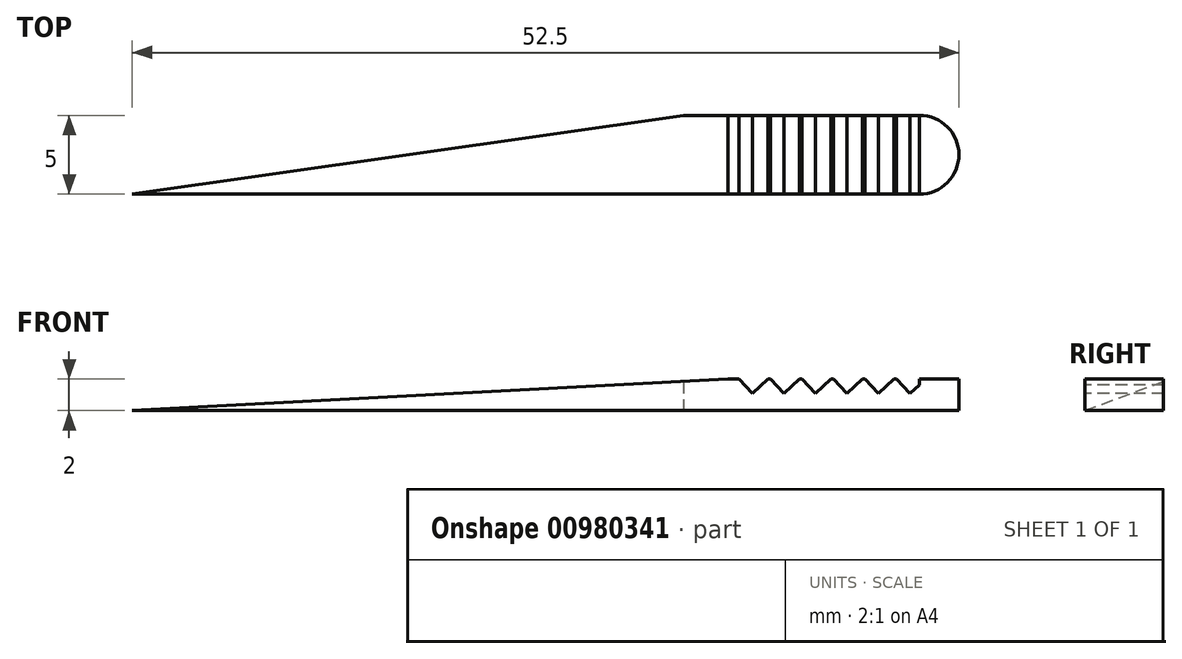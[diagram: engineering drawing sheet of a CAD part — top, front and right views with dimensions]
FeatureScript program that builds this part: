
annotation { "Feature Type Name" : "Feature", "Feature Type Description" : "" }
export const myFeature = defineFeature(function(context is Context, id is Id, definition is map)
    precondition{}
    {
        {
            var Q0;
            Q0=qCreatedBy(makeId("Top.planeOp"),FACE);
            var sketch = newSketch(context, id + "F0", { "sketchPlane" : qUnion([Q0])});
            skLineSegment(sketch, "E0", {"start": v(-50, 0) * mm, "end": v(0, 0) * mm});
            skLineSegment(sketch, "E1", {"start": v(0, 5) * mm, "end": v(-15, 5) * mm});
            skLineSegment(sketch, "E2", {"start": v(-15, 5) * mm, "end": v(-50, 0) * mm});
            skArc(sketch, "E3", {"start": v(0, 0) * mm, "mid": v(2.5, 2.5) * mm, "end": v(0, 5) * mm});
            skSolve(sketch);
        }
        {
            var Q0;
            Q0=makeQuery(id+"F0.imprint","IMPRINT",FACE,{"disambiguationData":[TD([[makeQuery(id+"F0.imprint","IMPRINT",EDGE,{"derivedFrom":sQuery(id+"F0.wireOp",EDGE,"E0")}),1.0]])]});
            extrude(context, id + "F1", {"entities" : qUnion([Q0]), "depth" : 2 * mm, "offsetDistance" : 25 * mm});
        }
        {
            var Q0;
            Q0=makeQuery(id+"F1.opExtrude","SWEPT_FACE",FACE,{"disambiguationData":[OSD([sQuery(id+"F0.wireOp",EDGE,"E0")])]});
            var sketch = newSketch(context, id + "F2", { "sketchPlane" : qUnion([Q0])});
            skLineSegment(sketch, "E4", {"start": v(-50, 0) * mm, "end": v(-12.17, 2) * mm});
            skSolve(sketch);
        }
        {
            var Q0;
            {var subQ0=sQuery(id+"F2.wireOp",EDGE,"E4");Q0=makeQuery(id+"F2.imprint","IMPRINT",FACE,{"disambiguationData":[TD([[makeQuery(id+"F2.imprint","IMPRINT",EDGE,{"derivedFrom":subQ0}),1.0]])]});}
            extrude(context, id + "F3", {"entities" : qUnion([Q0]), "operationType" : NewBodyOperationType.REMOVE, "oppositeDirection" : true, "depth" : 5 * mm, "offsetDistance" : 25 * mm});
        }
        {
            var Q0;
            Q0=makeQuery(id+"F1.opExtrude","SWEPT_FACE",FACE,{"disambiguationData":[OSD([sQuery(id+"F0.wireOp",EDGE,"E0")])]});
            var sketch = newSketch(context, id + "F4", { "sketchPlane" : qUnion([Q0])});
            skLineSegment(sketch, "E5", {"start": v(-11.47, 2) * mm, "end": v(-10.6, 1.07) * mm});
            skLineSegment(sketch, "E6", {"start": v(-10.6, 1.07) * mm, "end": v(-9.62, 2) * mm});
            skLineSegment(sketch, "E7.1.0.0", {"start": v(-9.47, 2) * mm, "end": v(-8.6, 1.07) * mm});
            skLineSegment(sketch, "E7.1.0.1", {"start": v(-8.6, 1.07) * mm, "end": v(-7.62, 2) * mm});
            skLineSegment(sketch, "E7.2.0.0", {"start": v(-7.47, 2) * mm, "end": v(-6.6, 1.07) * mm});
            skLineSegment(sketch, "E7.2.0.1", {"start": v(-6.6, 1.07) * mm, "end": v(-5.62, 2) * mm});
            skLineSegment(sketch, "E7.3.0.0", {"start": v(-5.47, 2) * mm, "end": v(-4.6, 1.07) * mm});
            skLineSegment(sketch, "E7.3.0.1", {"start": v(-4.6, 1.07) * mm, "end": v(-3.62, 2) * mm});
            skLineSegment(sketch, "E7.4.0.0", {"start": v(-3.47, 2) * mm, "end": v(-2.6, 1.07) * mm});
            skLineSegment(sketch, "E7.4.0.1", {"start": v(-2.6, 1.07) * mm, "end": v(-1.62, 2) * mm});
            skLineSegment(sketch, "E7.5.0.0", {"start": v(-1.47, 2) * mm, "end": v(-0.6, 1.07) * mm});
            skLineSegment(sketch, "E7.5.0.1", {"start": v(-0.6, 1.07) * mm, "end": v(0.38, 2) * mm});
            skLineSegment(sketch, "E7.direction1", {"start": v(-10.6, 1.07) * mm, "end": v(-8.6, 1.07) * mm, "construction": true});
            skSolve(sketch);
        }
        {
            var Q0;
            {var subQ0=sQuery(id+"F4.wireOp",EDGE,"E5");Q0=makeQuery(id+"F4.imprint","IMPRINT",FACE,{"disambiguationData":[TD([[makeQuery(id+"F4.imprint","IMPRINT",EDGE,{"derivedFrom":subQ0}),1.0]])]});}
            var Q1;
            {var subQ0=sQuery(id+"F4.wireOp",EDGE,"E7.1.0.0");Q1=makeQuery(id+"F4.imprint","IMPRINT",FACE,{"disambiguationData":[TD([[makeQuery(id+"F4.imprint","IMPRINT",EDGE,{"derivedFrom":subQ0}),1.0]])]});}
            var Q2;
            {var subQ0=sQuery(id+"F4.wireOp",EDGE,"E7.2.0.0");Q2=makeQuery(id+"F4.imprint","IMPRINT",FACE,{"disambiguationData":[TD([[makeQuery(id+"F4.imprint","IMPRINT",EDGE,{"derivedFrom":subQ0}),1.0]])]});}
            var Q3;
            {var subQ0=sQuery(id+"F4.wireOp",EDGE,"E7.3.0.0");Q3=makeQuery(id+"F4.imprint","IMPRINT",FACE,{"disambiguationData":[TD([[makeQuery(id+"F4.imprint","IMPRINT",EDGE,{"derivedFrom":subQ0}),1.0]])]});}
            var Q4;
            {var subQ0=sQuery(id+"F4.wireOp",EDGE,"E7.4.0.0");Q4=makeQuery(id+"F4.imprint","IMPRINT",FACE,{"disambiguationData":[TD([[makeQuery(id+"F4.imprint","IMPRINT",EDGE,{"derivedFrom":subQ0}),1.0]])]});}
            var Q5;
            {var subQ0=sQuery(id+"F4.wireOp",EDGE,"E7.5.0.0");Q5=makeQuery(id+"F4.imprint","IMPRINT",FACE,{"disambiguationData":[TD([[makeQuery(id+"F4.imprint","IMPRINT",EDGE,{"derivedFrom":subQ0}),1.0]])]});}
            extrude(context, id + "F5", {"entities" : qUnion([Q0, Q1, Q2, Q3, Q4, Q5]), "operationType" : NewBodyOperationType.REMOVE, "oppositeDirection" : true, "depth" : 5 * mm, "offsetDistance" : 25 * mm});
        }
    });
